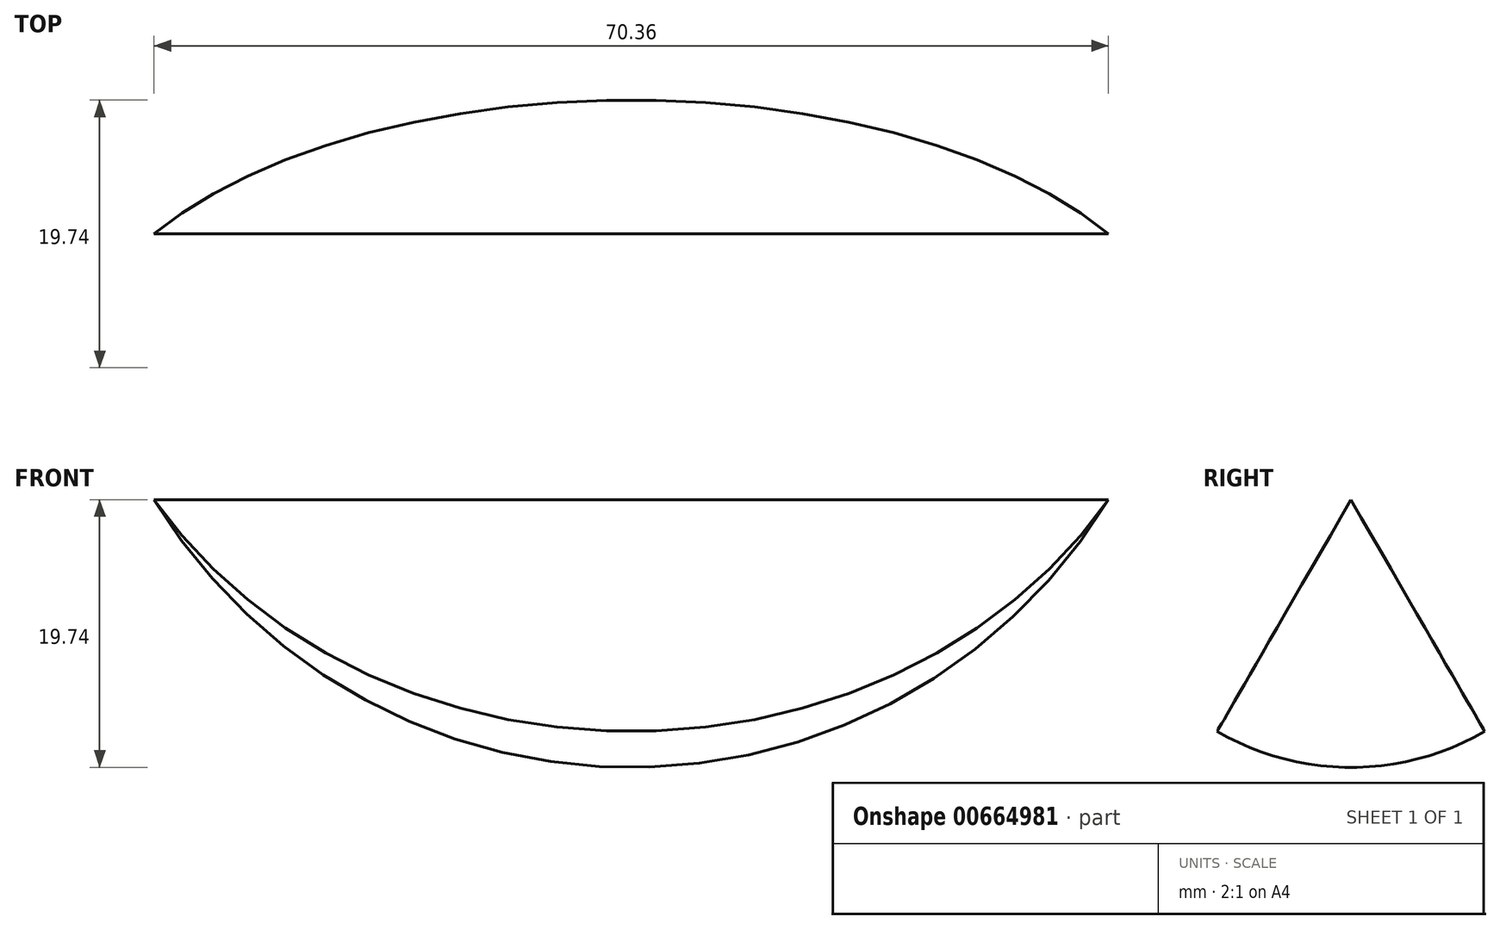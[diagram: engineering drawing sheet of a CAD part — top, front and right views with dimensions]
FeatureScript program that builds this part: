
annotation { "Feature Type Name" : "Feature", "Feature Type Description" : "" }
export const myFeature = defineFeature(function(context is Context, id is Id, definition is map)
    precondition{}
    {
        {
            var Q0;
            Q0=qCreatedBy(makeId("Front.planeOp"),FACE);
            var sketch = newSketch(context, id + "F0", { "sketchPlane" : qUnion([Q0])});
            skLineSegment(sketch, "E0", {"start": v(0, 0) * mm, "end": v(70.36, 0) * mm});
            skArc(sketch, "E1", {"start": v(0, 0) * mm, "mid": v(35.18, -19.74) * mm, "end": v(70.36, 0) * mm});
            skSolve(sketch);
        }
        {
            var Q0;
            Q0=makeQuery(id+"F0.imprint","IMPRINT",FACE,{"disambiguationData":[TD([[makeQuery(id+"F0.imprint","IMPRINT",EDGE,{"derivedFrom":sQuery(id+"F0.wireOp",EDGE,"E0")}),-1.0]])]});
            var Q1;
            Q1=sQuery(id+"F0.wireOp",EDGE,"E0");
            revolve(context, id + "F1", {"entities" : qUnion([Q0]), "axis" : qUnion([Q1]), "revolveType" : RevolveType.TWO_DIRECTIONS, "oppositeDirection" : true, "angle" : 30 * degree, "angleBack" : 330 * degree});
        }
    });
